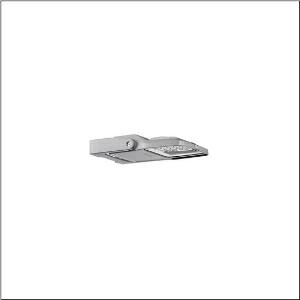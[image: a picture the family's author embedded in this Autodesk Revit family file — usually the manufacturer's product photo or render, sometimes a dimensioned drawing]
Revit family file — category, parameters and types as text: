
# Revit family: floodlight_fl_21_iq_micro___pl43_5xa7761a4a2a_9599
name_source: partatom
category: Lighting Fixtures
units: mm (PartAtom-declared; Revit-internal decimal feet)

## family parameters
Cut with Voids When Loaded = No
Host = Face
Light Source = No
Part Type = Normal
Room Calculation Point = No
Round Connector Dimension = Use Diameter
Shared = No

## types (1)
- --- (1 x LED, 3170 lm, 23.1 W, 4000K)
    Apparent Load = 23 VA
    CIE Flux Codes = 29 80 99 100 100
    Color Rendering = 70
    Color Temperature = 4000K
    Default Elevation = 1800 mm
    Description = Floodlight FL 21 iQ micro, floodlight, primary light control with lens, of PMMA, primary optical cover: protective disc, of toughened safety glass, transparent, light distribution: PL43, light emission: direct distribution, installation type: surface-mounted, lamps: LED, High Power LED, rated values: 3.170lm | 23,1W | 137,2lm/W (begin service life); end service life: 3.170lm | 23,8W; at 50% lumin. flux: 1.585lm | 11W | 144,1lm/W, colour temperature: 4000K, colour rendering: CRI > 70, light colour: 740, light setting 1 begin service life: 100% | 3.170lm | 23,1W | 137,2lm/W | 4.000K, light setting 1 end service life: 23,8W, further light settings possible, control: optimised constant luminous flux control (CLO 2.0), Desk-Remote (wireless, voltage-free reading and setting of iQ features in the workshop via application-optimized NFC function/RFID function), Light-Fading, Smart-Wire, Night-Set, Lumen-Switch, Temp-Guard, Auto-Match, pre-setting: linear dimming characteristic, with terminal, 6-pole, mains connection: 220..240V, AC, 50/60Hz, luminaire housing, of diecast aluminium, powder-coated, SITECO metallic grey (DB 702S), corrosivity category C5 mid according to DIN EN ISO 12944suitable for swimming poolschlorine-resistant, sealing non-destructively replaceable, design bracket, of diecast aluminium, powder-coated, SITECO metallic grey (DB 702S), protection rating (complete): IP66, insulation class (complete): insulation class II (safety insulation), certification: CE, ENEC, VDE, protection symbol: D, impact resistance: IK07, permissible operating ambient temperature: -40..+40°C, permissible operating ambient temperature for outdoor applications: -40..+50°C, standard: DIN EN 12944, LABS conformity tested according to VDMA 24364:2018-05, packaging unit: 1 piece

Light Distribution: PL43
    Height = 65 mm
    Lamp = 1 x LED
    Lamp Light Flux = 3170 lm
    Lamp Power = 23.1 W
    Lamp count = 1
    Length = 312 mm
    Luminous efficacy = 137 lm/W
    Manufacturer = Siteco
    ModVariant = No
    Model = 5XA7761A4A2A
    Mounting Place = Wall
    Mounting Type = Surface mounted
    Number of Poles = 1
    OnlyDefault = Yes
    Power Factor = 1
    Product Name = Floodlight FL 21 iQ micro | PL43
    Product group = floodlight | wall mounted
    ProductGroupID = 2002
    Protection Class = Protection class II
    Protection Degree = IP 66
    RLX_Detail_Level = 1
    RLX_Emergency_Light_Flux = 0 lm
    RLX_Emergency_Type = 0
    RLX_Emergency_Type_DB = No
    RlxData = <blob elided: 98037 chars, md5=f2e9f776>
    Socket = socket
    Standby Power = 0 W
    System Light Flux = 3170 lm
    System Power = 23 W
    Type Comments = factory setting: luminous flux: 100 % | dim-lin: 254 | 455 mA
    Type Image = l_1006878.jpg
    URL = http://relux.com
    VarID = @adj_177797
    Voltage = 0 V
    Weight = 0.00 kg
    Width = 230 mm

## geometry (parser evidence)
native form markers: Blend x4, Sweep x10
no freeform markers — native parametric forms only
